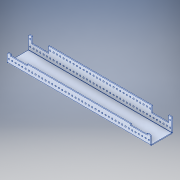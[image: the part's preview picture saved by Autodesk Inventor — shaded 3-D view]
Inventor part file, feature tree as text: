
AUTODESK INVENTOR PART (.ipt)
format: ipt  version: 2017 (Build 210142000, 142)  size: 332,288 bytes
history: native  units: in
note: dims shown in document units (in); Inventor stores cm internally (conversion verified against a paired STEP export)
features: other x5, reference x2, extrude x1, chamfer x1, sketch x1
ambient origin geometry x8: Origin, YZ Plane, XZ Plane, XY Plane, X Axis, Y Axis, Z Axis, Center Point
bodies: Solid1 (feature_tree)
feature tree (10):
  extrude  "Extrusion1"  Depth=0.5in
  chamfer  "Chamfer1"  Distance=10.0in
  sketch  "Sketch1"  dims[d0=1.0in d1=0.0in d2=0.5in d3=10.0in d4=1.0in d5=28.0in d6=9.5in d7=0.125in d8=0.125in d9=45.0deg]
  reference  "Reference1"
  reference  "Reference2"
  other  "LPattern4"
  other  "<userpath>\Documents\Inventor\2017 Robot\Robot Chassis.iam"
  other  "Robot Chassis.iam"
  other  "am-2951a_AM14U3_Outside_Plate:1"
  other  "am-2952a_AM14U3_Inside_Plate:1"
